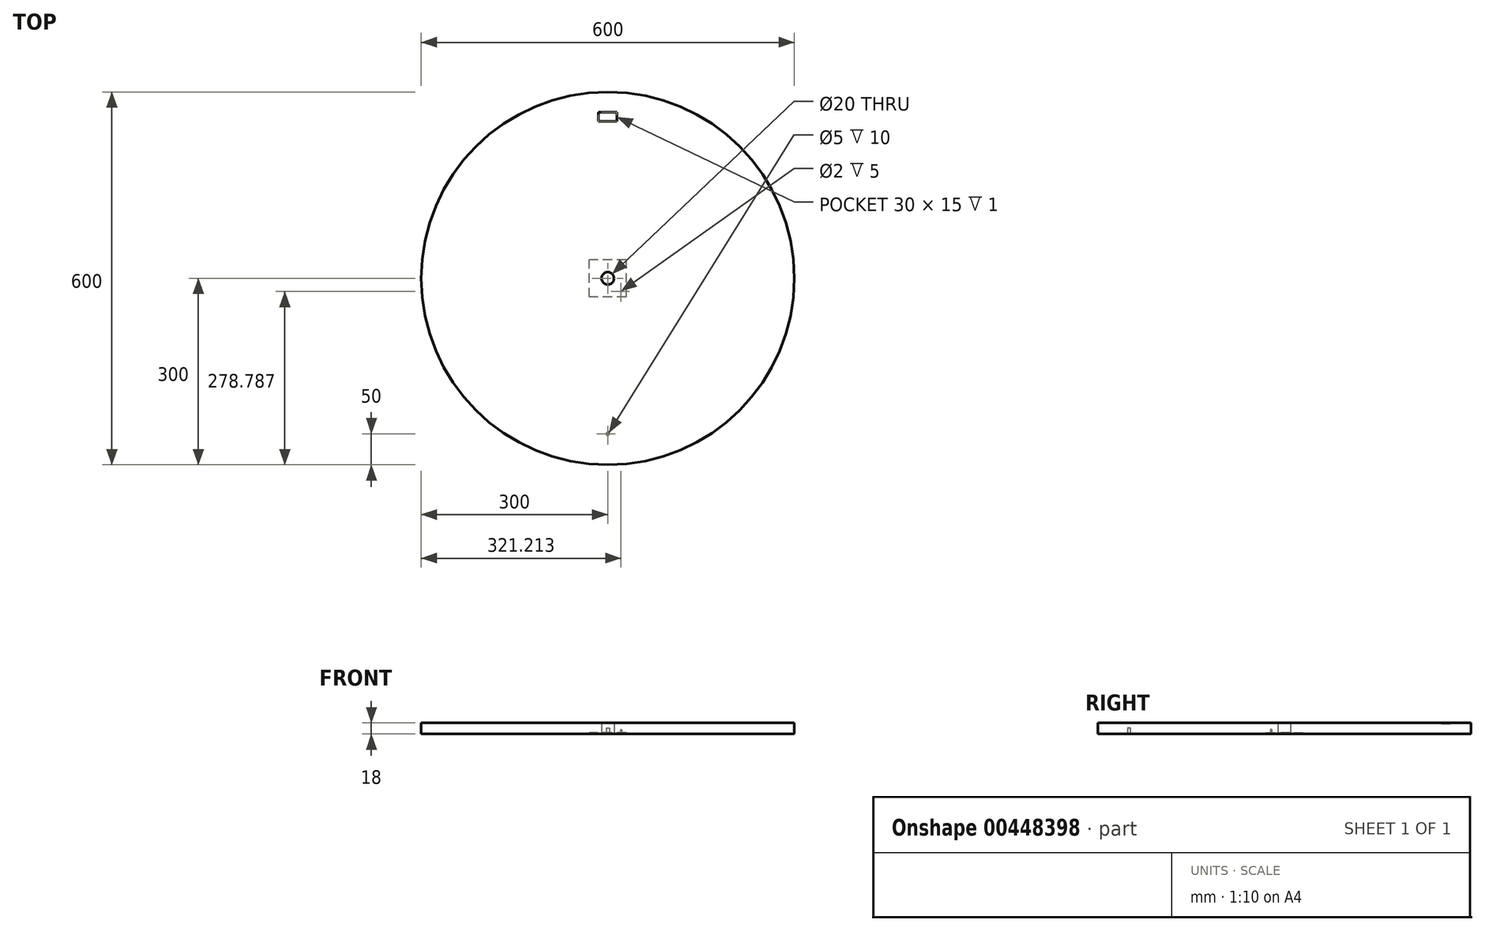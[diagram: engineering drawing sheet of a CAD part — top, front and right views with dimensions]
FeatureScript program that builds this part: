
annotation { "Feature Type Name" : "Feature", "Feature Type Description" : "" }
export const myFeature = defineFeature(function(context is Context, id is Id, definition is map)
    precondition{}
    {
        {
            var Q0;
            Q0=qCreatedBy(makeId("Top.planeOp"),FACE);
            var sketch = newSketch(context, id + "F0", { "sketchPlane" : qUnion([Q0])});
            skCircle(sketch, "E0", {"center": v(0, 0) * mm, "radius": 300 * mm});
            skCircle(sketch, "E1", {"center": v(0, 0) * mm, "radius": 10 * mm});
            skSolve(sketch);
        }
        {
            var Q0;
            Q0=makeQuery(id+"F0.imprint","IMPRINT",FACE,{"disambiguationData":[TD([[makeQuery(id+"F0.imprint","IMPRINT",EDGE,{"derivedFrom":sQuery(id+"F0.wireOp",EDGE,"E0")}),1.0]])]});
            extrude(context, id + "F1", {"entities" : qUnion([Q0]), "depth" : 18 * mm});
        }
        {
            var Q0;
            Q0=makeQuery(id+"F1.opExtrude","CAP_FACE",FACE,{"disambiguationData":[OSD([sQuery(id+"F0.wireOp",EDGE,"E0"),sQuery(id+"F0.wireOp",EDGE,"E1")])],"isStart":true});
            var sketch = newSketch(context, id + "F2", { "sketchPlane" : qUnion([Q0])});
            skCircle(sketch, "E2", {"center": v(0, 0) * mm, "radius": 250 * mm, "construction": true});
            skCircle(sketch, "E3", {"center": v(0, 250) * mm, "radius": 2.5 * mm});
            skSolve(sketch);
        }
        {
            var Q0;
            Q0=makeQuery(id+"F2.imprint","IMPRINT",FACE,{"disambiguationData":[TD([[makeQuery(id+"F2.imprint","IMPRINT",EDGE,{"derivedFrom":sQuery(id+"F2.wireOp",EDGE,"E3")}),1.0]])]});
            extrude(context, id + "F3", {"entities" : qUnion([Q0]), "operationType" : NewBodyOperationType.REMOVE, "oppositeDirection" : true, "depth" : 10 * mm});
        }
        {
            var Q0;
            Q0=makeQuery(id+"F1.opExtrude","CAP_FACE",FACE,{"disambiguationData":[OSD([sQuery(id+"F0.wireOp",EDGE,"E0"),sQuery(id+"F0.wireOp",EDGE,"E1")])],"isStart":true});
            var sketch = newSketch(context, id + "F4", { "sketchPlane" : qUnion([Q0])});
            skLineSegment(sketch, "E4.bottom", {"start": v(30, 30) * mm, "end": v(-30, 30) * mm});
            skLineSegment(sketch, "E4.top", {"start": v(30, -30) * mm, "end": v(-30, -30) * mm});
            skLineSegment(sketch, "E4.left", {"start": v(30, 30) * mm, "end": v(30, -30) * mm});
            skLineSegment(sketch, "E4.right", {"start": v(-30, 30) * mm, "end": v(-30, -30) * mm});
            skPoint(sketch, "E4.middle", {"position": v(0, 0) * mm});
            skSolve(sketch);
        }
        {
            var Q0;
            Q0 = qSketchRegion(id + "F4", true);
            extrude(context, id + "F5", {"entities" : qUnion([Q0]), "operationType" : NewBodyOperationType.REMOVE, "oppositeDirection" : true, "depth" : 2 * mm});
        }
        {
            var Q0;
            Q0=makeQuery(id+"F5.boolean.opBoolean","COPY",FACE,{"derivedFrom":makeQuery(id+"F5.opExtrude","CAP_FACE",FACE,{"disambiguationData":[OSD([sQuery(id+"F4.wireOp",EDGE,"E4.bottom"),sQuery(id+"F4.wireOp",EDGE,"E4.top"),sQuery(id+"F4.wireOp",EDGE,"E4.left"),sQuery(id+"F4.wireOp",EDGE,"E4.right")])],"isStart":false})});
            var sketch = newSketch(context, id + "F6", { "sketchPlane" : qUnion([Q0])});
            skCircle(sketch, "E5", {"center": v(0, 0) * mm, "radius": 30 * mm, "construction": true});
            skCircle(sketch, "E6", {"center": v(21.21, 21.21) * mm, "radius": 1 * mm});
            skLineSegment(sketch, "E7", {"start": v(0, 0) * mm, "end": v(21.21, 21.21) * mm, "construction": true});
            skSolve(sketch);
        }
        {
            var Q0;
            Q0 = qSketchRegion(id + "F6", true);
            extrude(context, id + "F7", {"entities" : qUnion([Q0]), "operationType" : NewBodyOperationType.REMOVE, "oppositeDirection" : true, "depth" : 5 * mm});
        }
        {
            var Q0;
            Q0=makeQuery(id+"F1.opExtrude","CAP_FACE",FACE,{"disambiguationData":[OSD([sQuery(id+"F0.wireOp",EDGE,"E0"),sQuery(id+"F0.wireOp",EDGE,"E1")])],"isStart":false});
            var sketch = newSketch(context, id + "F8", { "sketchPlane" : qUnion([Q0])});
            skCircle(sketch, "E8", {"center": v(0, 0) * mm, "radius": 260 * mm, "construction": true});
            skLineSegment(sketch, "E9.bottom", {"start": v(15, 252.5) * mm, "end": v(-15, 252.5) * mm});
            skLineSegment(sketch, "E9.top", {"start": v(15, 267.5) * mm, "end": v(-15, 267.5) * mm});
            skLineSegment(sketch, "E9.left", {"start": v(15, 252.5) * mm, "end": v(15, 267.5) * mm});
            skLineSegment(sketch, "E9.right", {"start": v(-15, 252.5) * mm, "end": v(-15, 267.5) * mm});
            skPoint(sketch, "E9.middle", {"position": v(0, 260) * mm});
            skSolve(sketch);
        }
        {
            var Q0;
            Q0=makeQuery(id+"F8.imprint","IMPRINT",FACE,{"disambiguationData":[TD([[makeQuery(id+"F8.imprint","IMPRINT",EDGE,{"derivedFrom":sQuery(id+"F8.wireOp",EDGE,"E9.bottom")}),-1.0]])]});
            extrude(context, id + "F9", {"entities" : qUnion([Q0]), "operationType" : NewBodyOperationType.REMOVE, "oppositeDirection" : true, "depth" : 1 * mm});
        }
    });
